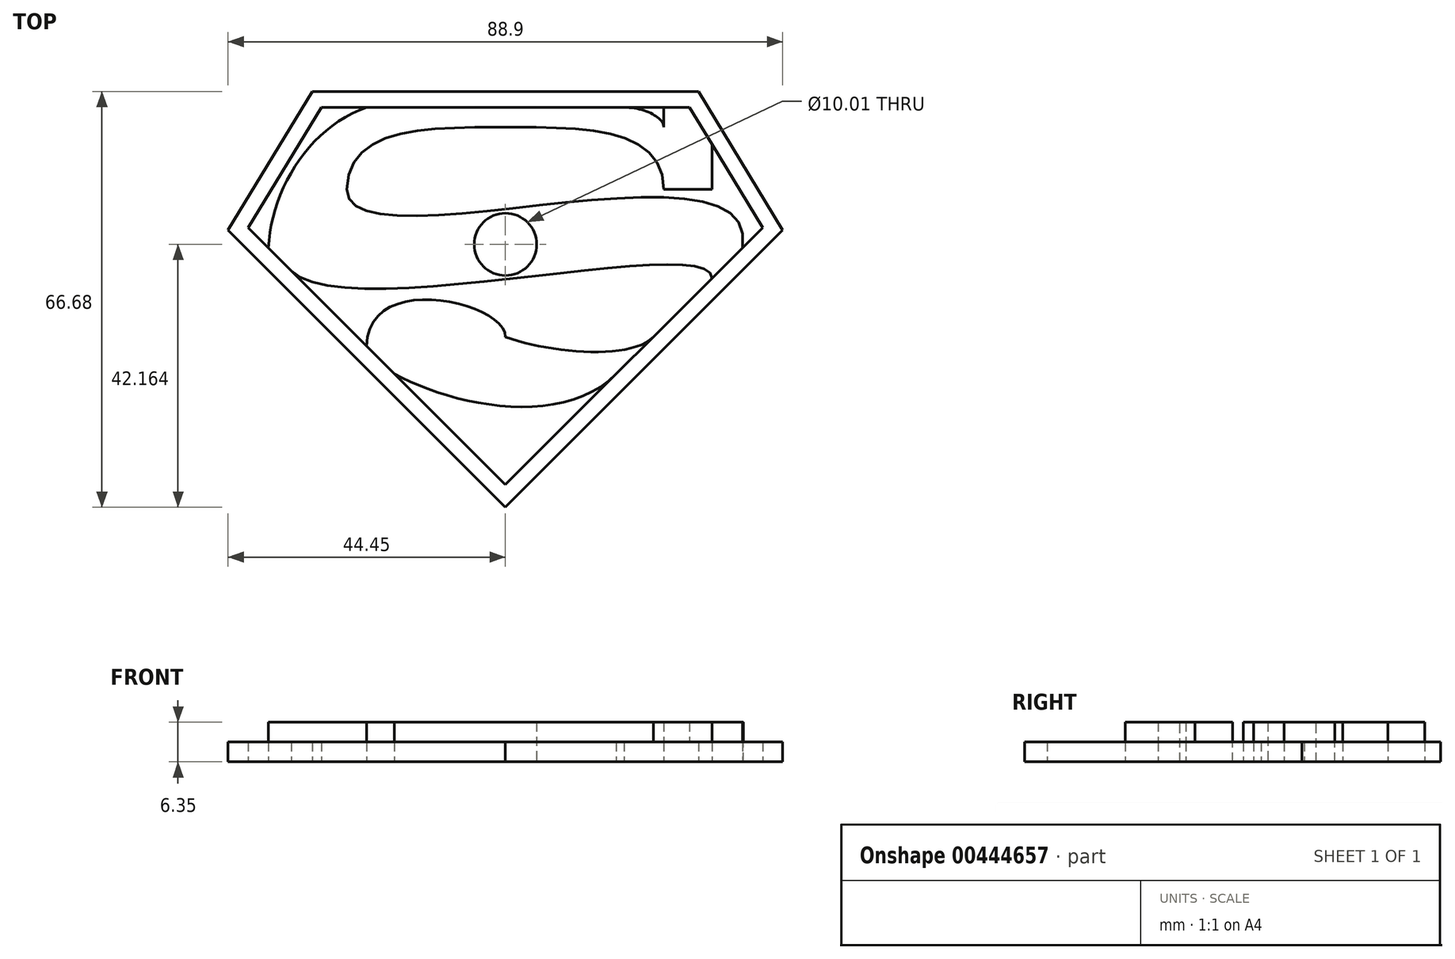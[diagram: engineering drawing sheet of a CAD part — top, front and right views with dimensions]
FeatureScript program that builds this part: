
annotation { "Feature Type Name" : "Feature", "Feature Type Description" : "" }
export const myFeature = defineFeature(function(context is Context, id is Id, definition is map)
    precondition{}
    {
        {
            var Q0;
            Q0=qCreatedBy(makeId("Top.planeOp"),FACE);
            var sketch = newSketch(context, id + "F0", { "sketchPlane" : qUnion([Q0])});
            skArc(sketch, "E0", {"start": v(-4.02, 2.97) * mm, "mid": v(0.53, -4.97) * mm, "end": v(3.3, 3.75) * mm, "construction": true});
            skCircle(sketch, "E1", {"center": v(0, 0) * mm, "radius": 38.1 * mm, "construction": true});
            skArc(sketch, "E2", {"start": v(-37.88, -1.46) * mm, "mid": v(-28.2, -0.99) * mm, "end": v(-36.94, 3.2) * mm, "construction": true});
            skArc(sketch, "E3", {"start": v(31.25, 4.64) * mm, "mid": v(30.02, -3.93) * mm, "end": v(38.05, -0.7) * mm, "construction": true});
            skCircle(sketch, "E4", {"center": v(0, 0) * mm, "radius": 44.45 * mm, "construction": true});
            skLineSegment(sketch, "E5", {"start": v(-30.95, 22.23) * mm, "end": v(30.95, 22.23) * mm});
            skLineSegment(sketch, "E6", {"start": v(30.95, 22.23) * mm, "end": v(44.45, 0) * mm});
            skLineSegment(sketch, "E7", {"start": v(44.45, 0) * mm, "end": v(0, -44.45) * mm});
            skLineSegment(sketch, "E8", {"start": v(0, -44.45) * mm, "end": v(-44.45, 0) * mm});
            skLineSegment(sketch, "E9", {"start": v(-44.45, 0) * mm, "end": v(-30.95, 22.23) * mm});
            skLineSegment(sketch, "E10.0", {"start": v(29.52, 19.69) * mm, "end": v(41.24, 0.39) * mm});
            skLineSegment(sketch, "E10.1", {"start": v(-29.52, 19.69) * mm, "end": v(29.52, 19.69) * mm});
            skLineSegment(sketch, "E10.2", {"start": v(41.24, 0.39) * mm, "end": v(0, -40.86) * mm});
            skLineSegment(sketch, "E10.3", {"start": v(0, -40.86) * mm, "end": v(-41.24, 0.39) * mm});
            skLineSegment(sketch, "E10.4", {"start": v(-41.24, 0.39) * mm, "end": v(-29.52, 19.69) * mm});
            skLineSegment(sketch, "E11", {"start": v(25.4, 56.12) * mm, "end": v(25.4, -51.2) * mm, "construction": true});
            skLineSegment(sketch, "E12", {"start": v(-75.36, 56.12) * mm, "end": v(-75.36, -51.2) * mm, "construction": true});
            skLineSegment(sketch, "E13", {"start": v(33.1, 56.12) * mm, "end": v(33.1, -51.38) * mm, "construction": true});
            skLineSegment(sketch, "E14", {"start": v(62.24, 6.52) * mm, "end": v(-46.25, 6.52) * mm, "construction": true});
            skLineSegment(sketch, "E15", {"start": v(33.1, 13.79) * mm, "end": v(33.1, 6.52) * mm});
            skLineSegment(sketch, "E16", {"start": v(33.1, 6.52) * mm, "end": v(25.4, 6.52) * mm});
            skPoint(sketch, "E17", {"position": v(25.4, 19.69) * mm});
            skLineSegment(sketch, "E18", {"start": v(62.16, -6.52) * mm, "end": v(-46.01, -6.52) * mm, "construction": true});
            skLineSegment(sketch, "E19.MirrorCS", {"start": v(-25.4, 56.12) * mm, "end": v(-25.4, -51.2) * mm, "construction": true});
            skPoint(sketch, "E20", {"position": v(-25.4, 19.69) * mm});
            skLineSegment(sketch, "E21", {"start": v(-47.42, 16.51) * mm, "end": v(83.12, 16.51) * mm, "construction": true});
            skPoint(sketch, "E22", {"position": v(0, 16.51) * mm});
            skFitSpline(sketch, "E23", {"points": [v(25.4, 6.52) * mm, v(0, 16.51) * mm, v(-25.4, 6.52) * mm], "startDerivative": vector(0, 59.92) * mm, "endDerivative": vector(0, -59.92) * mm});
            skFitSpline(sketch, "E24", {"points": [v(-25.4, 6.52) * mm, v(38, -2.87) * mm], "startDerivative": vector(0, -39.14) * mm, "endDerivative": vector(-9.83, -58.13) * mm});
            skLineSegment(sketch, "E25", {"start": v(25.4, 19.69) * mm, "end": v(25.4, 16.5) * mm});
            skPoint(sketch, "E26", {"position": v(19.05, 19.69) * mm});
            skFitSpline(sketch, "E27", {"points": [v(25.4, 16.51) * mm, v(19.05, 19.69) * mm], "startDerivative": vector(0, 4.76) * mm, "endDerivative": vector(-9.52, 0) * mm});
            skLineSegment(sketch, "E28", {"start": v(20.03, 18.1) * mm, "end": v(35.05, 18.1) * mm, "construction": true});
            skLineSegment(sketch, "E29", {"start": v(-22.23, 56.55) * mm, "end": v(-22.23, -50.97) * mm, "construction": true});
            skFitSpline(sketch, "E30", {"points": [v(-22.23, 19.69) * mm, v(-38, -2.87) * mm], "startDerivative": vector(-27.66, -9.52) * mm, "endDerivative": vector(-1.36, -28.17) * mm});
            skFitSpline(sketch, "E31", {"points": [v(-34.33, -6.52) * mm, v(33.1, -7.76) * mm], "startDerivative": vector(26.8, -26.8) * mm, "endDerivative": vector(0, -23.27) * mm});
            skFitSpline(sketch, "E32", {"points": [v(-22.23, -18.63) * mm, v(0, -17.15) * mm], "startDerivative": vector(0, 36.33) * mm, "endDerivative": vector(0, -17.15) * mm});
            skLineSegment(sketch, "E33", {"start": v(-45.65, -17.15) * mm, "end": v(53.5, -17.15) * mm, "construction": true});
            skLineSegment(sketch, "E34", {"start": v(-5.68, -11.43) * mm, "end": v(5.68, -11.43) * mm, "construction": true});
            skFitSpline(sketch, "E35", {"points": [v(0, -17.15) * mm, v(23.71, -17.15) * mm], "startDerivative": vector(21.6, -7.62) * mm, "endDerivative": vector(11.43, 11.43) * mm});
            skLineSegment(sketch, "E36", {"start": v(16.49, -20.96) * mm, "end": v(24.73, -20.96) * mm, "construction": true});
            skLineSegment(sketch, "E37", {"start": v(3.3, -19.69) * mm, "end": v(11.46, -19.69) * mm, "construction": true});
            skLineSegment(sketch, "E38", {"start": v(7.2, -17.68) * mm, "end": v(7.2, -22.75) * mm, "construction": true});
            skLineSegment(sketch, "E39", {"start": v(-17.78, -15.34) * mm, "end": v(-17.78, -30.8) * mm, "construction": true});
            skLineSegment(sketch, "E40.MirrorCS", {"start": v(17.78, -15.34) * mm, "end": v(17.78, -30.8) * mm, "construction": true});
            skFitSpline(sketch, "E41", {"points": [v(-17.78, -23.08) * mm, v(17.78, -23.08) * mm], "startDerivative": vector(26.6, -14.61) * mm, "endDerivative": vector(26.73, 26.73) * mm});
            skCircle(sketch, "E42", {"center": v(0, -2.29) * mm, "radius": 5 * mm});
            skSolve(sketch);
        }
        {
            var Q0;
            Q0=makeQuery(id+"F0.imprint","IMPRINT",FACE,{"disambiguationData":[TD([[makeQuery(id+"F0.imprint","IMPRINT",EDGE,{"derivedFrom":sQuery(id+"F0.wireOp",EDGE,"E5")}),-1.0]])]});
            extrude(context, id + "F1", {"entities" : qUnion([Q0]), "depth" : 3.17 * mm});
        }
        {
            var Q0;
            {var subQ2=sQuery(id+"F0.wireOp",EDGE,"E15");Q0=makeQuery(id+"F0.imprint","IMPRINT",FACE,{"disambiguationData":[TD([[makeQuery(id+"F0.imprint","IMPRINT",EDGE,{"derivedFrom":subQ2}),-1.0]])]});}
            var Q1;
            {var subQ1=sQuery(id+"F0.wireOp",EDGE,"E32");Q1=makeQuery(id+"F0.imprint","IMPRINT",FACE,{"disambiguationData":[TD([[makeQuery(id+"F0.imprint","IMPRINT",EDGE,{"derivedFrom":subQ1}),-1.0]])]});}
            extrude(context, id + "F2", {"entities" : qUnion([Q0, Q1]), "operationType" : NewBodyOperationType.ADD, "depth" : 6.35 * mm});
        }
    });
